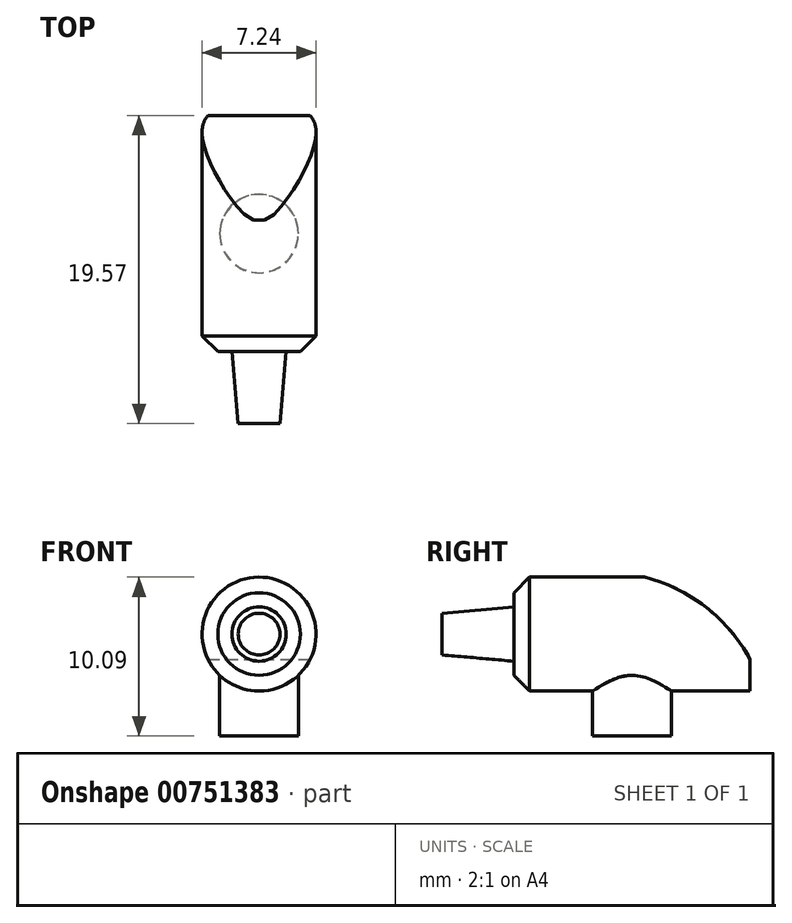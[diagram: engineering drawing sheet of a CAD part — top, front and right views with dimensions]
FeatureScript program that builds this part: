
annotation { "Feature Type Name" : "Feature", "Feature Type Description" : "" }
export const myFeature = defineFeature(function(context is Context, id is Id, definition is map)
    precondition{}
    {
        {
            var Q0;
            Q0=qCreatedBy(makeId("Top.planeOp"),FACE);
            var sketch = newSketch(context, id + "F0", { "sketchPlane" : qUnion([Q0])});
            skCircle(sketch, "E0", {"center": v(0, 0) * mm, "radius": 2.5 * mm});
            skSolve(sketch);
        }
        {
            var Q0;
            Q0 = qSketchRegion(id + "F0", true);
            extrude(context, id + "F1", {"entities" : qUnion([Q0]), "depth" : 7 * mm, "offsetDistance" : 25 * mm});
        }
        {
            var Q0;
            Q0=qCreatedBy(makeId("Front.planeOp"),FACE);
            var sketch = newSketch(context, id + "F2", { "sketchPlane" : qUnion([Q0])});
            skCircle(sketch, "E1", {"center": v(0, 6.47) * mm, "radius": 3.62 * mm});
            skSolve(sketch);
        }
        {
            var Q0;
            Q0=makeQuery(id+"F2.imprint","IMPRINT",FACE,{"disambiguationData":[TD([[makeQuery(id+"F2.imprint","IMPRINT",EDGE,{"derivedFrom":sQuery(id+"F2.wireOp",EDGE,"E1")}),1.0]])]});
            extrude(context, id + "F3", {"entities" : qUnion([Q0]), "operationType" : NewBodyOperationType.ADD, "endBound" : BoundingType.SYMMETRIC, "depth" : 15 * mm, "offsetDistance" : 25 * mm});
        }
        {
            var Q0;
            Q0=qCreatedBy(makeId("Right.planeOp"),FACE);
            var sketch = newSketch(context, id + "F4", { "sketchPlane" : qUnion([Q0])});
            skArc(sketch, "E2", {"start": v(7.92, 4) * mm, "mid": v(4.76, 8.13) * mm, "end": v(0, 10.26) * mm});
            skLineSegment(sketch, "E3", {"start": v(0, 10.26) * mm, "end": v(7.96, 10.26) * mm});
            skLineSegment(sketch, "E4", {"start": v(7.96, 10.26) * mm, "end": v(7.92, 4) * mm});
            skSolve(sketch);
        }
        {
            var Q0;
            Q0=makeQuery(id+"F4.imprint","IMPRINT",FACE,{"disambiguationData":[TD([[makeQuery(id+"F4.imprint","IMPRINT",EDGE,{"derivedFrom":sQuery(id+"F4.wireOp",EDGE,"E2")}),-1.0]])]});
            extrude(context, id + "F5", {"entities" : qUnion([Q0]), "operationType" : NewBodyOperationType.REMOVE, "endBound" : BoundingType.SYMMETRIC, "oppositeDirection" : true, "depth" : 25 * mm, "offsetDistance" : 25 * mm});
        }
        {
            var Q0;
            Q0=makeQuery(id+"F3.opExtrude","CAP_EDGE",EDGE,{"disambiguationData":[OSD([sQuery(id+"F2.wireOp",EDGE,"E1")])],"isStart":false});
            chamfer(context, id + "F6", {"entities" : qUnion([Q0]), "width" : 1 * mm, "tangentPropagation" : true});
        }
        {
            var Q0;
            Q0=makeQuery(id+"F3.opExtrude","CAP_FACE",FACE,{"disambiguationData":[OSD([sQuery(id+"F2.wireOp",EDGE,"E1")])],"isStart":false});
            var sketch = newSketch(context, id + "F7", { "sketchPlane" : qUnion([Q0])});
            skCircle(sketch, "E5", {"center": v(0, 6.47) * mm, "radius": 1.72 * mm});
            skSolve(sketch);
        }
        {
            var Q0;
            Q0=makeQuery(id+"F7.imprint","IMPRINT",FACE,{"disambiguationData":[TD([[makeQuery(id+"F7.imprint","IMPRINT",EDGE,{"derivedFrom":sQuery(id+"F7.wireOp",EDGE,"E5")}),1.0]])]});
            extrude(context, id + "F8", {"entities" : qUnion([Q0]), "operationType" : NewBodyOperationType.ADD, "depth" : 4.57 * mm, "offsetDistance" : 25 * mm, "hasDraft" : true, "draftAngle" : 5 * degree, "draftPullDirection" : true});
        }
    });
